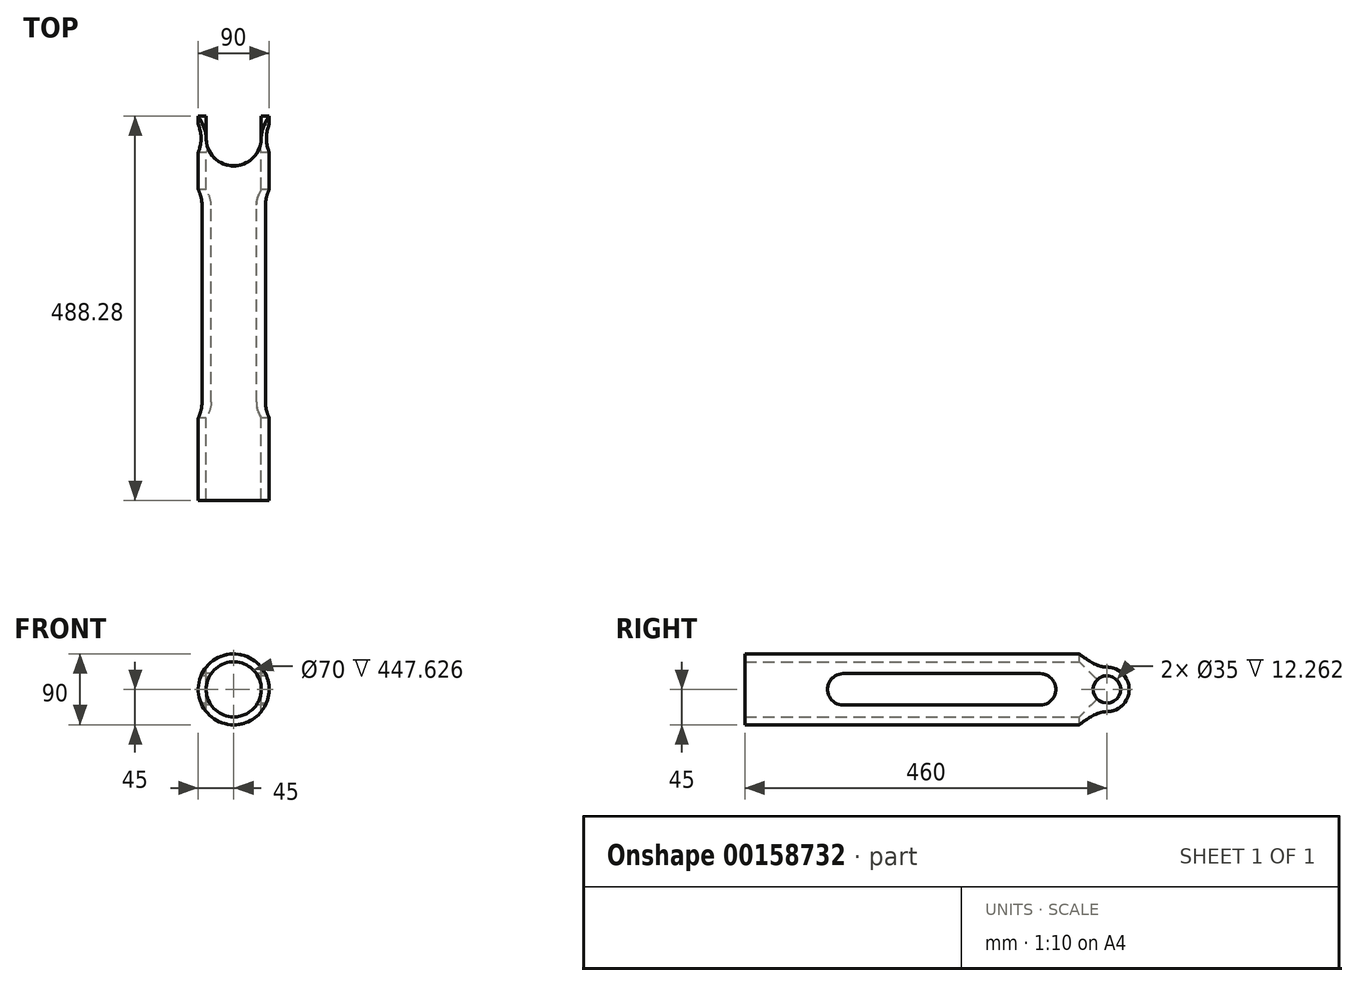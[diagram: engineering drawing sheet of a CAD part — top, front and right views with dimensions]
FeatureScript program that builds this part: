
annotation { "Feature Type Name" : "Feature", "Feature Type Description" : "" }
export const myFeature = defineFeature(function(context is Context, id is Id, definition is map)
    precondition{}
    {
        {
            var Q0;
            Q0=qCreatedBy(makeId("Front.planeOp"),FACE);
            var sketch = newSketch(context, id + "F0", { "sketchPlane" : qUnion([Q0])});
            skCircle(sketch, "E0", {"center": v(0, 0) * mm, "radius": 45 * mm});
            skCircle(sketch, "E1.0", {"center": v(0, 0) * mm, "radius": 35 * mm});
            skSolve(sketch);
        }
        {
            var Q0;
            Q0=makeQuery(id+"F0.imprint","IMPRINT",FACE,{"disambiguationData":[TD([[makeQuery(id+"F0.imprint","IMPRINT",EDGE,{"derivedFrom":sQuery(id+"F0.wireOp",EDGE,"E0")}),1.0]])]});
            extrude(context, id + "F1", {"entities" : qUnion([Q0]), "depth" : 500 * mm});
        }
        {
            var Q0;
            Q0=qCreatedBy(makeId("Right.planeOp"),FACE);
            var sketch = newSketch(context, id + "F2", { "sketchPlane" : qUnion([Q0])});
            skCircle(sketch, "E2", {"center": v(-125, 0) * mm, "radius": 20 * mm});
            skCircle(sketch, "E3", {"center": v(-375, 0) * mm, "radius": 20 * mm});
            skLineSegment(sketch, "E4", {"start": v(-375, 20) * mm, "end": v(-125, 20) * mm});
            skLineSegment(sketch, "E5", {"start": v(-375, -20) * mm, "end": v(-125, -20) * mm});
            skSolve(sketch);
        }
        {
            var Q0;
            Q0 = qSketchRegion(id + "F2", true);
            extrude(context, id + "F3", {"entities" : qUnion([Q0]), "operationType" : NewBodyOperationType.REMOVE, "endBound" : BoundingType.SYMMETRIC, "depth" : 200 * mm});
        }
        {
            var Q0;
            Q0=qCreatedBy(makeId("Top.planeOp"),FACE);
            var sketch = newSketch(context, id + "F4", { "sketchPlane" : qUnion([Q0])});
            skArc(sketch, "E6", {"start": v(-35, -40) * mm, "mid": v(0, -75) * mm, "end": v(35, -40) * mm});
            skLineSegment(sketch, "E7", {"start": v(-35, -40) * mm, "end": v(-35, 0) * mm});
            skLineSegment(sketch, "E8", {"start": v(35, -40) * mm, "end": v(35, 0) * mm});
            skLineSegment(sketch, "E9", {"start": v(35, 0) * mm, "end": v(-35, 0) * mm});
            skSolve(sketch);
        }
        {
            var Q0;
            Q0 = qSketchRegion(id + "F4", true);
            extrude(context, id + "F5", {"entities" : qUnion([Q0]), "operationType" : NewBodyOperationType.REMOVE, "endBound" : BoundingType.SYMMETRIC, "oppositeDirection" : true, "depth" : 200 * mm});
        }
        {
            var Q0;
            Q0=qCreatedBy(makeId("Right.planeOp"),FACE);
            var sketch = newSketch(context, id + "F6", { "sketchPlane" : qUnion([Q0])});
            skCircle(sketch, "E10", {"center": v(-40, 0) * mm, "radius": 17.5 * mm});
            skSolve(sketch);
        }
        {
            var Q0;
            Q0 = qSketchRegion(id + "F6", true);
            extrude(context, id + "F7", {"entities" : qUnion([Q0]), "operationType" : NewBodyOperationType.REMOVE, "endBound" : BoundingType.SYMMETRIC, "oppositeDirection" : true, "depth" : 200 * mm});
        }
        {
            var Q0;
            Q0=makeQuery(id+"F5.boolean.opBoolean","COPY",FACE,{"derivedFrom":makeQuery(id+"F5.opExtrude","SWEPT_FACE",FACE,{"disambiguationData":[OSD([sQuery(id+"F4.wireOp",EDGE,"E7")])]})});
            var sketch = newSketch(context, id + "F8", { "sketchPlane" : qUnion([Q0])});
            skPoint(sketch, "E11", {"position": v(-40, 0) * mm});
            skArc(sketch, "E12", {"start": v(-40, -28.28) * mm, "mid": v(-11.72, 0) * mm, "end": v(-40, 28.28) * mm});
            skLineSegment(sketch, "E13", {"start": v(-40, 28.28) * mm, "end": v(0, 28.28) * mm});
            skLineSegment(sketch, "E14", {"start": v(0, 28.28) * mm, "end": v(0, -28.28) * mm});
            skLineSegment(sketch, "E15", {"start": v(0, -28.28) * mm, "end": v(-40, -28.28) * mm});
            skPoint(sketch, "E16", {"position": v(-22.5, 0) * mm});
            skSolve(sketch);
        }
        {
            var Q0;
            Q0 = qSketchRegion(id + "F8", true);
            extrude(context, id + "F9", {"entities" : qUnion([Q0]), "operationType" : NewBodyOperationType.REMOVE, "endBound" : BoundingType.SYMMETRIC, "oppositeDirection" : true, "depth" : 200 * mm});
        }
        {
            var Q0;
            Q0=qCreatedBy(makeId("Front.planeOp"),FACE);
            var Q1;
            Q1=makeQuery(id+"F1.opExtrude","CAP_FACE",FACE,{"disambiguationData":[OSD([sQuery(id+"F0.wireOp",EDGE,"E0"),sQuery(id+"F0.wireOp",EDGE,"E1.0")])],"isStart":false});
            cPlane(context, id + "F10", {"entities" : qUnion([Q0, Q1]), "cplaneType" : CPlaneType.MID_PLANE, "offset" : 25 * mm, "width" : 150 * mm, "height" : 150 * mm});
        }
    });
